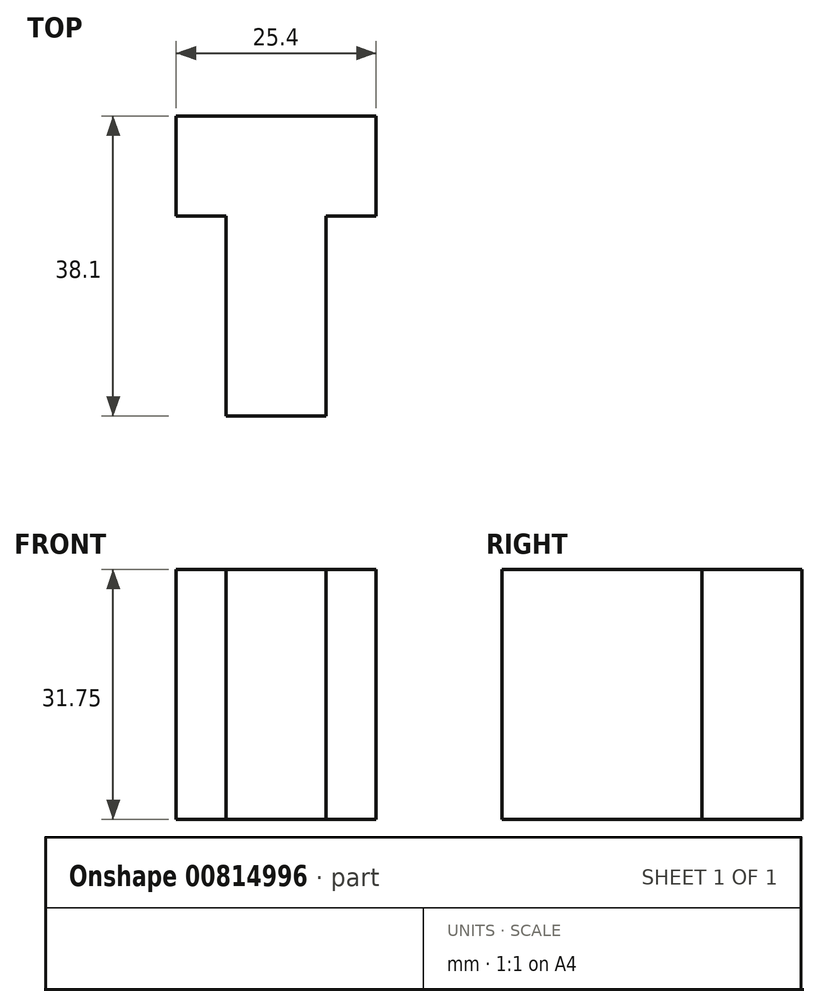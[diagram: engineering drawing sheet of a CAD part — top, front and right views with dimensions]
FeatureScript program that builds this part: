
annotation { "Feature Type Name" : "Feature", "Feature Type Description" : "" }
export const myFeature = defineFeature(function(context is Context, id is Id, definition is map)
    precondition{}
    {
        {
            var Q0;
            Q0=qCreatedBy(makeId("Top.planeOp"),FACE);
            var sketch = newSketch(context, id + "F0", { "sketchPlane" : qUnion([Q0])});
            skLineSegment(sketch, "E0", {"start": v(-57.4, 0) * mm, "end": v(-44.7, 0) * mm});
            skLineSegment(sketch, "E1", {"start": v(-44.7, 0) * mm, "end": v(-44.7, 25.4) * mm});
            skLineSegment(sketch, "E2", {"start": v(-57.4, 0) * mm, "end": v(-57.4, 25.4) * mm});
            skLineSegment(sketch, "E3", {"start": v(-44.7, 25.4) * mm, "end": v(-38.35, 25.4) * mm});
            skLineSegment(sketch, "E4", {"start": v(-57.4, 25.4) * mm, "end": v(-63.75, 25.4) * mm});
            skLineSegment(sketch, "E5", {"start": v(-63.75, 25.4) * mm, "end": v(-63.75, 38.1) * mm});
            skLineSegment(sketch, "E6", {"start": v(-38.35, 25.4) * mm, "end": v(-38.35, 38.1) * mm});
            skLineSegment(sketch, "E7", {"start": v(-63.75, 38.1) * mm, "end": v(-38.35, 38.1) * mm});
            skSolve(sketch);
        }
        {
            var Q0;
            Q0=makeQuery(id+"F0.imprint","IMPRINT",FACE,{"disambiguationData":[TD([[makeQuery(id+"F0.imprint","IMPRINT",EDGE,{"derivedFrom":sQuery(id+"F0.wireOp",EDGE,"E0")}),1.0]])]});
            extrude(context, id + "F1", {"entities" : qUnion([Q0]), "depth" : 31.75 * mm, "offsetDistance" : 25.4 * mm});
        }
    });
